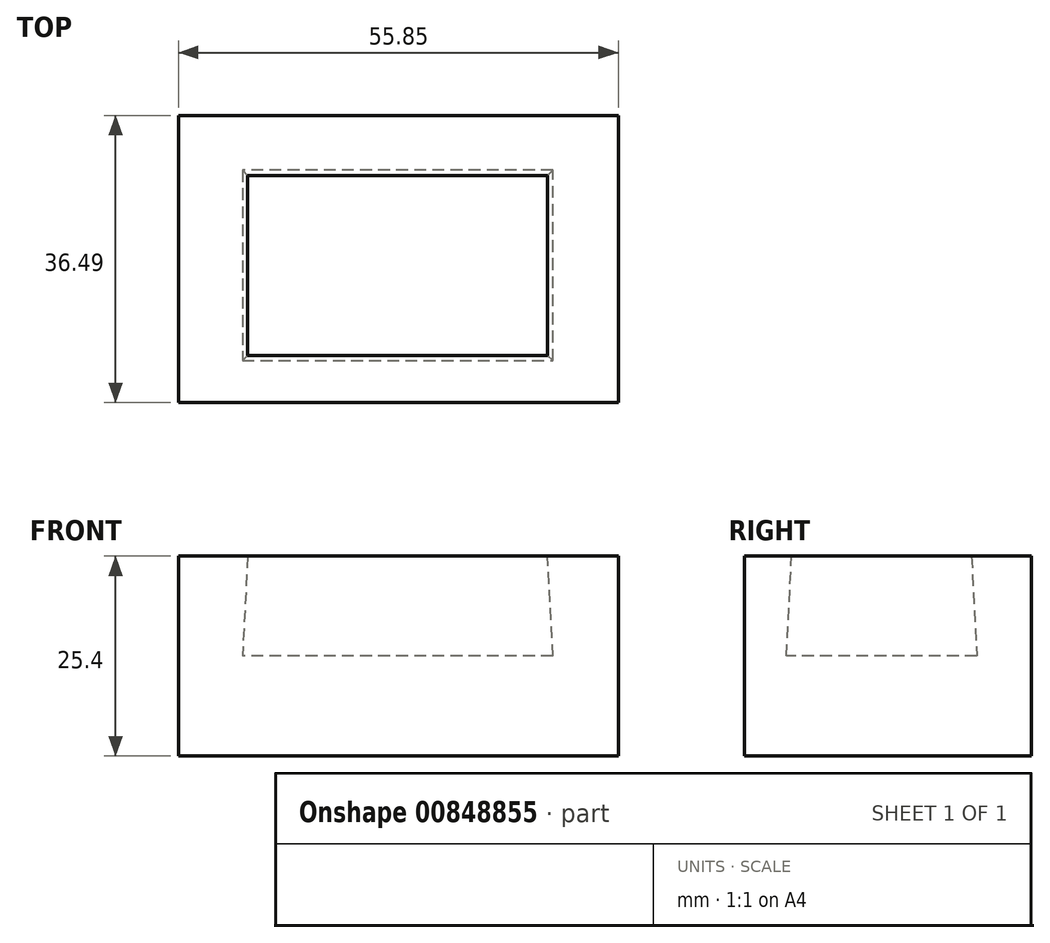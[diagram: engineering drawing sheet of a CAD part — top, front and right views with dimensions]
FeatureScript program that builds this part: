
annotation { "Feature Type Name" : "Feature", "Feature Type Description" : "" }
export const myFeature = defineFeature(function(context is Context, id is Id, definition is map)
    precondition{}
    {
        {
            var Q0;
            Q0=qCreatedBy(makeId("Top.planeOp"),FACE);
            var sketch = newSketch(context, id + "F0", { "sketchPlane" : qUnion([Q0])});
            skLineSegment(sketch, "E0.bottom", {"start": v(0, 0) * mm, "end": v(55.85, 0) * mm});
            skLineSegment(sketch, "E0.top", {"start": v(0, 36.5) * mm, "end": v(55.85, 36.5) * mm});
            skLineSegment(sketch, "E0.left", {"start": v(0, 0) * mm, "end": v(0, 36.5) * mm});
            skLineSegment(sketch, "E0.right", {"start": v(55.85, 0) * mm, "end": v(55.85, 36.5) * mm});
            skSolve(sketch);
        }
        {
            var Q0;
            Q0 = qSketchRegion(id + "F0", true);
            extrude(context, id + "F1", {"entities" : qUnion([Q0]), "depth" : 25.4 * mm, "offsetDistance" : 25.4 * mm});
        }
        {
            var Q0;
            Q0=makeQuery(id+"F1.opExtrude","CAP_FACE",FACE,{"disambiguationData":[OSD([sQuery(id+"F0.wireOp",EDGE,"E0.bottom"),sQuery(id+"F0.wireOp",EDGE,"E0.top"),sQuery(id+"F0.wireOp",EDGE,"E0.left"),sQuery(id+"F0.wireOp",EDGE,"E0.right")])],"isStart":false});
            var sketch = newSketch(context, id + "F2", { "sketchPlane" : qUnion([Q0])});
            skLineSegment(sketch, "E1.bottom", {"start": v(8.77, 28.87) * mm, "end": v(46.87, 28.87) * mm});
            skLineSegment(sketch, "E1.top", {"start": v(8.77, 6.01) * mm, "end": v(46.87, 6.01) * mm});
            skLineSegment(sketch, "E1.left", {"start": v(8.77, 28.87) * mm, "end": v(8.77, 6.01) * mm});
            skLineSegment(sketch, "E1.right", {"start": v(46.87, 28.87) * mm, "end": v(46.87, 6.01) * mm});
            skSolve(sketch);
        }
        {
            var Q0;
            Q0 = qSketchRegion(id + "F2", true);
            extrude(context, id + "F3", {"entities" : qUnion([Q0]), "operationType" : NewBodyOperationType.REMOVE, "oppositeDirection" : true, "depth" : 12.7 * mm, "offsetDistance" : 25.4 * mm, "hasDraft" : true, "draftAngle" : 3 * degree});
        }
    });
